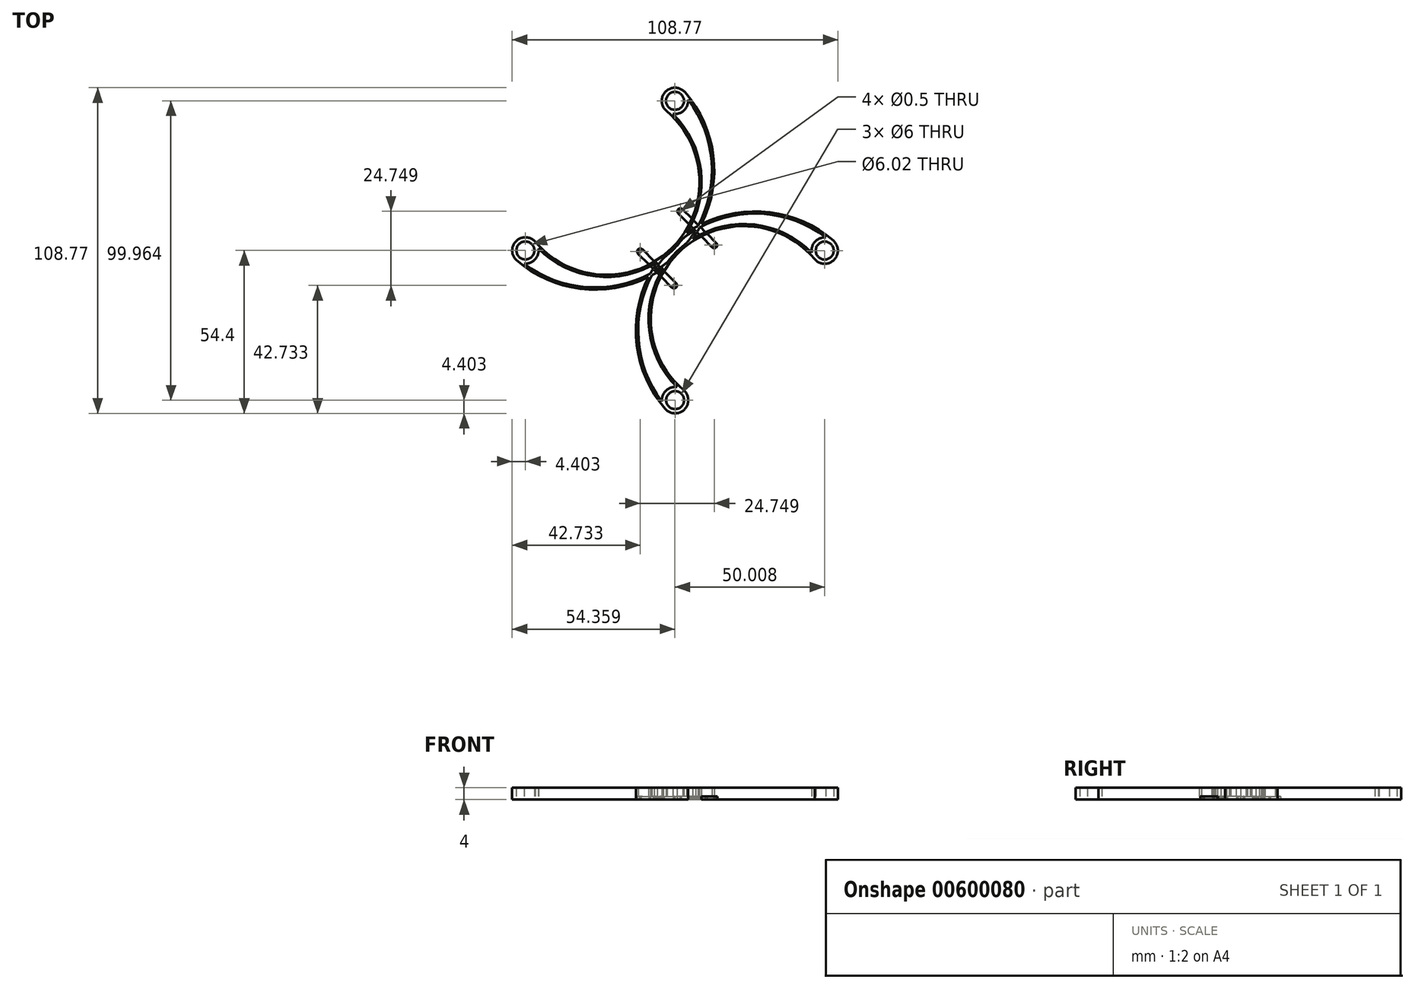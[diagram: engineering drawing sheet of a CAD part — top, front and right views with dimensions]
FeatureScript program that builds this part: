
annotation { "Feature Type Name" : "Feature", "Feature Type Description" : "" }
export const myFeature = defineFeature(function(context is Context, id is Id, definition is map)
    precondition{}
    {
        {
            var Q0;
            Q0=qCreatedBy(makeId("Top.planeOp"),FACE);
            var sketch = newSketch(context, id + "F0", { "sketchPlane" : qUnion([Q0])});
            skCircle(sketch, "E0.3.0", {"center": v(-0.04, 49.97) * mm, "radius": 3 * mm});
            skArc(sketch, "E1", {"start": v(-46.7, 2.9) * mm, "mid": v(-0.97, 0.94) * mm, "end": v(-2.94, 46.66) * mm});
            skArc(sketch, "E2", {"start": v(-52.88, -3.32) * mm, "mid": v(-31.7, -12.79) * mm, "end": v(-8.83, -8.83) * mm});
            skArc(sketch, "E3.trimOffspring", {"start": v(8.8, 8.8) * mm, "mid": v(12.75, 31.66) * mm, "end": v(3.28, 52.86) * mm});
            skPoint(sketch, "E4.orphan", {"position": v(-52.38, -2.74) * mm});
            skPoint(sketch, "E5.orphan", {"position": v(-47.27, 2.4) * mm});
            skPoint(sketch, "E6.orphan", {"position": v(-2.4, 47.27) * mm});
            skPoint(sketch, "E7.orphan", {"position": v(2.74, 52.38) * mm});
            skArc(sketch, "E8.trimOffspring", {"start": v(-10.4, -5.66) * mm, "mid": v(-10.37, -5.65) * mm, "end": v(-10.34, -5.64) * mm});
            skArc(sketch, "E9.trimOffspring", {"start": v(-10.35, -5.7) * mm, "mid": v(-10.37, -5.68) * mm, "end": v(-10.4, -5.66) * mm});
            skArc(sketch, "E10.0", {"start": v(-45.65, 0.7) * mm, "mid": v(-26.59, -8.65) * mm, "end": v(-5.89, -3.9) * mm});
            skArc(sketch, "E11.0", {"start": v(-50.4, -4.38) * mm, "mid": v(-30.32, -12.18) * mm, "end": v(-9.16, -8.16) * mm});
            skArc(sketch, "E12.0", {"start": v(-9.16, -8.16) * mm, "mid": v(-8.7, -7.92) * mm, "end": v(-8.22, -7.67) * mm});
            skArc(sketch, "E13.0", {"start": v(-46.7, 2.9) * mm, "mid": v(-53.12, 3.1) * mm, "end": v(-52.88, -3.32) * mm});
            skArc(sketch, "E14.0", {"start": v(3.28, 52.86) * mm, "mid": v(-3.15, 53.09) * mm, "end": v(-2.94, 46.66) * mm});
            skArc(sketch, "E15.trimOffspring", {"start": v(-50.4, -4.38) * mm, "mid": v(-46.78, -3) * mm, "end": v(-45.65, 0.7) * mm});
            skArc(sketch, "E16.trimOffspring", {"start": v(-0.75, 45.62) * mm, "mid": v(2.96, 46.75) * mm, "end": v(4.34, 50.36) * mm});
            skArc(sketch, "E17.trimOffspring", {"start": v(-4.2, -2.75) * mm, "mid": v(-0.57, 0.34) * mm, "end": v(2.56, 3.94) * mm});
            skArc(sketch, "E18.MirrorCS", {"start": v(-5.7, -10.35) * mm, "mid": v(-5.68, -10.37) * mm, "end": v(-5.66, -10.4) * mm});
            skArc(sketch, "E19.MirrorCS", {"start": v(45.62, -0.75) * mm, "mid": v(46.75, 2.96) * mm, "end": v(50.36, 4.34) * mm});
            skArc(sketch, "E20.MirrorCS", {"start": v(-3.32, -52.88) * mm, "mid": v(-12.79, -31.7) * mm, "end": v(-8.83, -8.83) * mm});
            skPoint(sketch, "E21.MirrorP", {"position": v(52.38, 2.74) * mm});
            skArc(sketch, "E22.MirrorCS", {"start": v(8.8, 8.8) * mm, "mid": v(31.66, 12.75) * mm, "end": v(52.86, 3.28) * mm});
            skArc(sketch, "E23.MirrorCS", {"start": v(-2.75, -4.2) * mm, "mid": v(0.34, -0.57) * mm, "end": v(3.94, 2.56) * mm});
            skArc(sketch, "E24.MirrorCS", {"start": v(-5.66, -10.4) * mm, "mid": v(-5.65, -10.37) * mm, "end": v(-5.64, -10.34) * mm});
            skArc(sketch, "E25.MirrorCS", {"start": v(0.7, -45.65) * mm, "mid": v(-8.65, -26.59) * mm, "end": v(-3.9, -5.89) * mm});
            skArc(sketch, "E26.MirrorCS", {"start": v(-4.38, -50.4) * mm, "mid": v(-12.18, -30.32) * mm, "end": v(-8.16, -9.16) * mm});
            skArc(sketch, "E27.MirrorCS", {"start": v(-4.38, -50.4) * mm, "mid": v(-3, -46.78) * mm, "end": v(0.7, -45.65) * mm});
            skPoint(sketch, "E28.MirrorP", {"position": v(2.4, -47.27) * mm});
            skPoint(sketch, "E29.MirrorP", {"position": v(-2.74, -52.38) * mm});
            skCircle(sketch, "E30.MirrorC", {"center": v(0, -50) * mm, "radius": 3 * mm});
            skArc(sketch, "E31.MirrorCS", {"start": v(52.86, 3.28) * mm, "mid": v(53.09, -3.15) * mm, "end": v(46.66, -2.94) * mm});
            skCircle(sketch, "E32.MirrorC", {"center": v(49.97, -0.04) * mm, "radius": 3 * mm});
            skArc(sketch, "E33.MirrorCS", {"start": v(2.9, -46.7) * mm, "mid": v(0.94, -0.97) * mm, "end": v(46.66, -2.94) * mm});
            skArc(sketch, "E34.MirrorCS", {"start": v(-8.16, -9.16) * mm, "mid": v(-7.92, -8.7) * mm, "end": v(-7.67, -8.22) * mm});
            skArc(sketch, "E35.MirrorCS", {"start": v(2.9, -46.7) * mm, "mid": v(3.1, -53.12) * mm, "end": v(-3.32, -52.88) * mm});
            skPoint(sketch, "E36.MirrorP", {"position": v(47.27, -2.4) * mm});
            skArc(sketch, "E37.trimOffspring", {"start": v(3.87, 5.85) * mm, "mid": v(5.72, 7.07) * mm, "end": v(7.63, 8.19) * mm});
            skArc(sketch, "E38.trimOffspring", {"start": v(5.85, 3.87) * mm, "mid": v(7.07, 5.72) * mm, "end": v(8.19, 7.63) * mm});
            skArc(sketch, "E39.trimOffspring", {"start": v(-8.22, -7.67) * mm, "mid": v(-7.1, -5.75) * mm, "end": v(-5.89, -3.9) * mm});
            skArc(sketch, "E40.trimOffspring", {"start": v(-6.95, -6.95) * mm, "mid": v(-5.54, -4.72) * mm, "end": v(-3.97, -2.6) * mm});
            skArc(sketch, "E41.trimOffspring", {"start": v(-7.67, -8.22) * mm, "mid": v(-5.75, -7.1) * mm, "end": v(-3.9, -5.89) * mm});
            skArc(sketch, "E42.trimOffspring", {"start": v(-6.95, -6.95) * mm, "mid": v(-4.72, -5.54) * mm, "end": v(-2.6, -3.97) * mm});
            skArc(sketch, "E43.trimOffspring", {"start": v(2.56, 3.94) * mm, "mid": v(4.69, 5.5) * mm, "end": v(6.92, 6.92) * mm});
            skArc(sketch, "E44.trimOffspring", {"start": v(3.94, 2.56) * mm, "mid": v(5.5, 4.69) * mm, "end": v(6.92, 6.92) * mm});
            skArc(sketch, "E45.trimOffspring", {"start": v(3.87, 5.85) * mm, "mid": v(8.62, 26.56) * mm, "end": v(-0.75, 45.62) * mm});
            skArc(sketch, "E46.trimOffspring", {"start": v(7.63, 8.19) * mm, "mid": v(12.2, 29.76) * mm, "end": v(4.34, 50.36) * mm});
            skArc(sketch, "E47.trimOffspring", {"start": v(8.19, 7.63) * mm, "mid": v(29.76, 12.2) * mm, "end": v(50.36, 4.34) * mm});
            skArc(sketch, "E48.trimOffspring", {"start": v(5.85, 3.87) * mm, "mid": v(26.56, 8.62) * mm, "end": v(45.62, -0.75) * mm});
            skCircle(sketch, "E49", {"center": v(-50, 0) * mm, "radius": 3 * mm});
            skSolve(sketch);
        }
        {
            var Q0;
            Q0=qCreatedBy(makeId("Top.planeOp"),FACE);
            var sketch = newSketch(context, id + "F1", { "sketchPlane" : qUnion([Q0])});
            skPoint(sketch, "E50", {"position": v(13.08, 1.77) * mm});
            skPoint(sketch, "E51", {"position": v(-11.67, -0.35) * mm});
            skLineSegment(sketch, "E52.0", {"start": v(-12.37, -1.06) * mm, "end": v(-6.72, -6.72) * mm});
            skLineSegment(sketch, "E53.MirrorCS", {"start": v(-10.96, 0.35) * mm, "end": v(-5.3, -5.3) * mm});
            skLineSegment(sketch, "E54.0", {"start": v(13.79, 2.47) * mm, "end": v(8.13, 8.13) * mm});
            skLineSegment(sketch, "E55.MirrorCS", {"start": v(12.37, 1.06) * mm, "end": v(6.72, 6.72) * mm});
            skArc(sketch, "E56", {"start": v(-10.96, 0.35) * mm, "mid": v(-12.37, 0.35) * mm, "end": v(-12.37, -1.06) * mm});
            skArc(sketch, "E57", {"start": v(12.37, 1.06) * mm, "mid": v(13.79, 1.06) * mm, "end": v(13.79, 2.47) * mm});
            skCircle(sketch, "E58", {"center": v(-11.67, -0.35) * mm, "radius": 0.25 * mm});
            skCircle(sketch, "E59", {"center": v(13.08, 1.77) * mm, "radius": 0.25 * mm});
            skLineSegment(sketch, "E60.MirrorCS", {"start": v(1.06, 12.37) * mm, "end": v(6.72, 6.72) * mm});
            skLineSegment(sketch, "E61.MirrorCS", {"start": v(2.47, 13.79) * mm, "end": v(8.13, 8.13) * mm});
            skArc(sketch, "E62.MirrorCS", {"start": v(1.06, 12.37) * mm, "mid": v(1.06, 13.79) * mm, "end": v(2.47, 13.79) * mm});
            skLineSegment(sketch, "E63.MirrorCS", {"start": v(0.35, -10.96) * mm, "end": v(-5.3, -5.3) * mm});
            skLineSegment(sketch, "E64.MirrorCS", {"start": v(-1.06, -12.37) * mm, "end": v(-6.72, -6.72) * mm});
            skArc(sketch, "E65.MirrorCS", {"start": v(0.35, -10.96) * mm, "mid": v(0.35, -12.37) * mm, "end": v(-1.06, -12.37) * mm});
            skCircle(sketch, "E66.MirrorC", {"center": v(-0.35, -11.67) * mm, "radius": 0.25 * mm});
            skCircle(sketch, "E67.MirrorC", {"center": v(1.77, 13.08) * mm, "radius": 0.25 * mm});
            skLineSegment(sketch, "E68", {"start": v(0, 0) * mm, "end": v(-9.92, 9.92) * mm});
            skLineSegment(sketch, "E69", {"start": v(0, 0) * mm, "end": v(11.08, 11.08) * mm});
            skSolve(sketch);
        }
        {
            var Q0;
            Q0=makeQuery(id+"F0.imprint","IMPRINT",FACE,{"disambiguationData":[TD([[makeQuery(id+"F0.imprint","IMPRINT",EDGE,{"derivedFrom":sQuery(id+"F0.wireOp",EDGE,"E0.3.0")}),-1.0]])]});
            extrude(context, id + "F2", {"entities" : qUnion([Q0]), "depth" : 4 * mm});
        }
        {
            var Q0;
            Q0=qSketchRegion(id+"F1",true);
            extrude(context, id + "F3", {"entities" : qUnion([Q0]), "operationType" : NewBodyOperationType.ADD, "depth" : 1 * mm});
        }
    });
